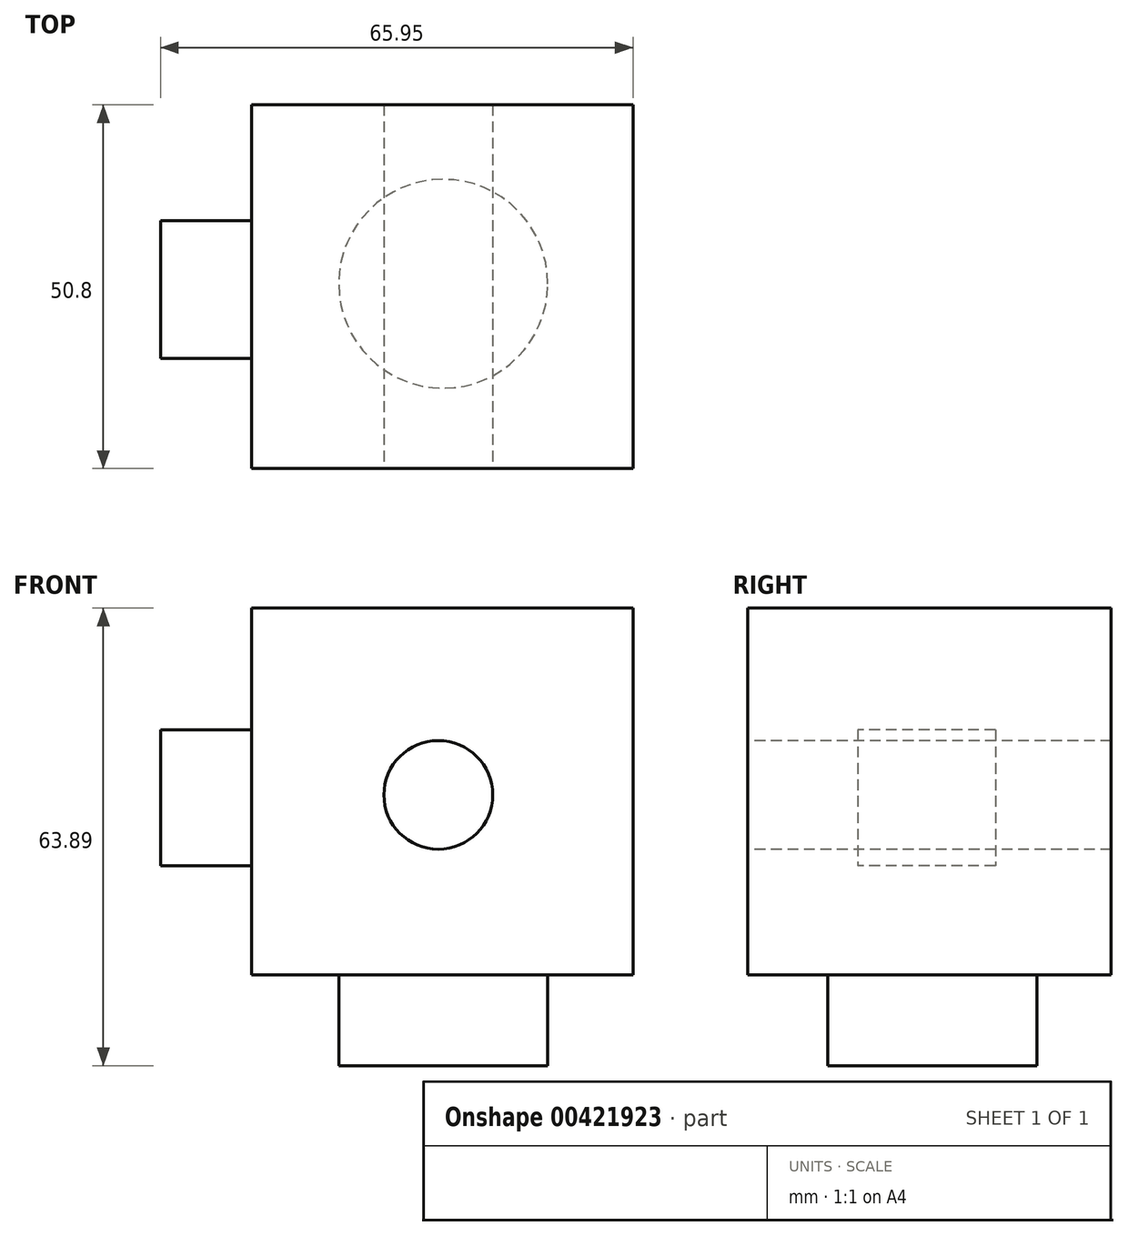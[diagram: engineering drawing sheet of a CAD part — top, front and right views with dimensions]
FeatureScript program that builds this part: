
annotation { "Feature Type Name" : "Feature", "Feature Type Description" : "" }
export const myFeature = defineFeature(function(context is Context, id is Id, definition is map)
    precondition{}
    {
        {
            var Q0;
            Q0=qCreatedBy(makeId("Front.planeOp"),FACE);
            var sketch = newSketch(context, id + "F0", { "sketchPlane" : qUnion([Q0])});
            skLineSegment(sketch, "E0.bottom", {"start": v(0, 0) * mm, "end": v(-53.25, 0) * mm});
            skLineSegment(sketch, "E0.top", {"start": v(0, 51.19) * mm, "end": v(-53.25, 51.19) * mm});
            skLineSegment(sketch, "E0.left", {"start": v(0, 0) * mm, "end": v(0, 51.19) * mm});
            skLineSegment(sketch, "E0.right", {"start": v(-53.25, 0) * mm, "end": v(-53.25, 51.19) * mm});
            skSolve(sketch);
        }
        {
            var Q0;
            Q0 = qSketchRegion(id + "F0", true);
            var Q1;
            Q1=makeQuery(id+"F0.imprint","IMPRINT",FACE,{"disambiguationData":[TD([[makeQuery(id+"F0.imprint","IMPRINT",EDGE,{"derivedFrom":sQuery(id+"F0.wireOp",EDGE,"E0.bottom")}),-1.0]])]});
            extrude(context, id + "F1", {"entities" : qUnion([Q0, Q1]), "depth" : 50.8 * mm});
        }
        {
            var Q0;
            Q0=makeQuery(id+"F1.opExtrude","CAP_FACE",FACE,{"disambiguationData":[OSD([sQuery(id+"F0.wireOp",EDGE,"E0.bottom"),sQuery(id+"F0.wireOp",EDGE,"E0.top"),sQuery(id+"F0.wireOp",EDGE,"E0.left"),sQuery(id+"F0.wireOp",EDGE,"E0.right")])],"isStart":false});
            var sketch = newSketch(context, id + "F2", { "sketchPlane" : qUnion([Q0])});
            skCircle(sketch, "E1", {"center": v(-27.17, 25.11) * mm, "radius": 7.6 * mm});
            skSolve(sketch);
        }
        {
            var Q0;
            Q0=makeQuery(id+"F2.imprint","IMPRINT",FACE,{"disambiguationData":[TD([[makeQuery(id+"F2.imprint","IMPRINT",EDGE,{"derivedFrom":sQuery(id+"F2.wireOp",EDGE,"E1")}),1.0]])]});
            extrude(context, id + "F3", {"entities" : qUnion([Q0]), "operationType" : NewBodyOperationType.REMOVE, "oppositeDirection" : true, "depth" : 50.8 * mm});
        }
        {
            var Q0;
            Q0=makeQuery(id+"F1.opExtrude","SWEPT_FACE",FACE,{"disambiguationData":[OSD([sQuery(id+"F0.wireOp",EDGE,"E0.right")])]});
            var sketch = newSketch(context, id + "F4", { "sketchPlane" : qUnion([Q0])});
            skLineSegment(sketch, "E2.bottom", {"start": v(16.2, 34.17) * mm, "end": v(35.4, 34.17) * mm});
            skLineSegment(sketch, "E2.top", {"start": v(16.2, 15.23) * mm, "end": v(35.4, 15.23) * mm});
            skLineSegment(sketch, "E2.left", {"start": v(16.2, 34.17) * mm, "end": v(16.2, 15.23) * mm});
            skLineSegment(sketch, "E2.right", {"start": v(35.4, 34.17) * mm, "end": v(35.4, 15.23) * mm});
            skSolve(sketch);
        }
        {
            var Q0;
            Q0=makeQuery(id+"F4.imprint","IMPRINT",FACE,{"disambiguationData":[TD([[makeQuery(id+"F4.imprint","IMPRINT",EDGE,{"derivedFrom":sQuery(id+"F4.wireOp",EDGE,"E2.bottom")}),-1.0]])]});
            extrude(context, id + "F5", {"entities" : qUnion([Q0]), "operationType" : NewBodyOperationType.ADD, "depth" : 12.7 * mm});
        }
        {
            var Q0;
            Q0=makeQuery(id+"F1.opExtrude","SWEPT_FACE",FACE,{"disambiguationData":[OSD([sQuery(id+"F0.wireOp",EDGE,"E0.bottom")])]});
            var sketch = newSketch(context, id + "F6", { "sketchPlane" : qUnion([Q0])});
            skCircle(sketch, "E3", {"center": v(-26.49, 24.98) * mm, "radius": 14.6 * mm});
            skSolve(sketch);
        }
        {
            var Q0;
            Q0=makeQuery(id+"F6.imprint","IMPRINT",FACE,{"disambiguationData":[TD([[makeQuery(id+"F6.imprint","IMPRINT",EDGE,{"derivedFrom":sQuery(id+"F6.wireOp",EDGE,"E3")}),1.0]])]});
            extrude(context, id + "F7", {"entities" : qUnion([Q0]), "operationType" : NewBodyOperationType.ADD, "depth" : 12.7 * mm});
        }
    });
